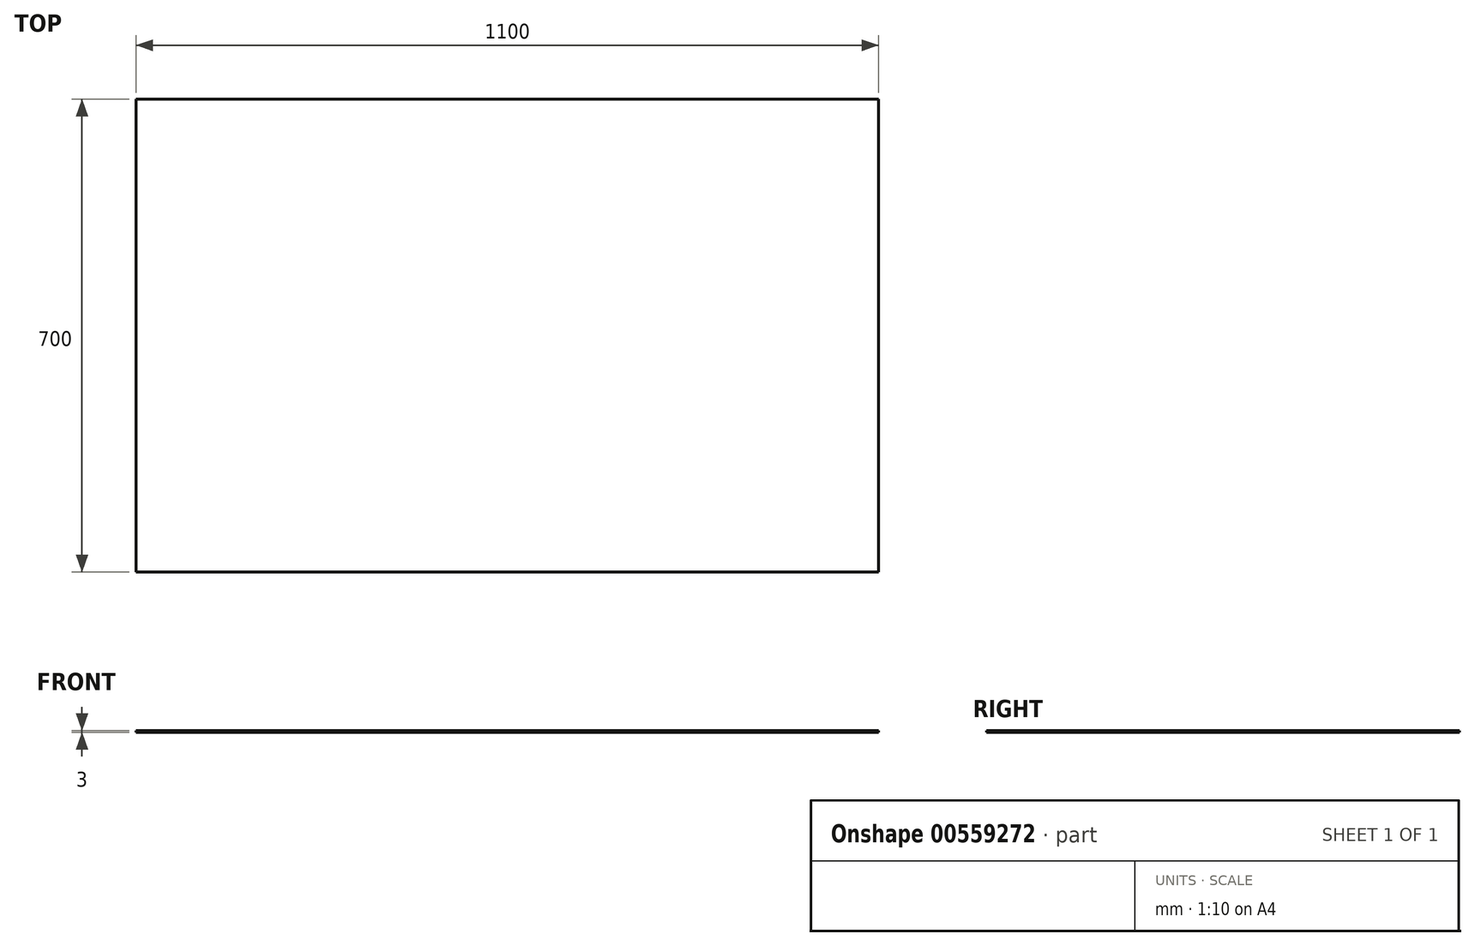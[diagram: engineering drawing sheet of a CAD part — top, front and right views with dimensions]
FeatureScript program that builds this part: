
annotation { "Feature Type Name" : "Feature", "Feature Type Description" : "" }
export const myFeature = defineFeature(function(context is Context, id is Id, definition is map)
    precondition{}
    {
        {
            var Q0;
            Q0=qCreatedBy(makeId("Top.planeOp"),FACE);
            var sketch = newSketch(context, id + "F0", { "sketchPlane" : qUnion([Q0])});
            skLineSegment(sketch, "E0.bottom", {"start": v(550, 350) * mm, "end": v(-550, 350) * mm});
            skLineSegment(sketch, "E0.top", {"start": v(550, -350) * mm, "end": v(-550, -350) * mm});
            skLineSegment(sketch, "E0.left", {"start": v(550, 350) * mm, "end": v(550, -350) * mm});
            skLineSegment(sketch, "E0.right", {"start": v(-550, 350) * mm, "end": v(-550, -350) * mm});
            skPoint(sketch, "E0.middle", {"position": v(0, 0) * mm});
            skSolve(sketch);
        }
        {
            var Q0;
            Q0=makeQuery(id+"F0.imprint","IMPRINT",FACE,{"disambiguationData":[TD([[makeQuery(id+"F0.imprint","IMPRINT",EDGE,{"derivedFrom":sQuery(id+"F0.wireOp",EDGE,"E0.bottom")}),1.0]])]});
            extrude(context, id + "F1", {"entities" : qUnion([Q0]), "depth" : 3 * mm, "offsetDistance" : 25 * mm});
        }
    });
